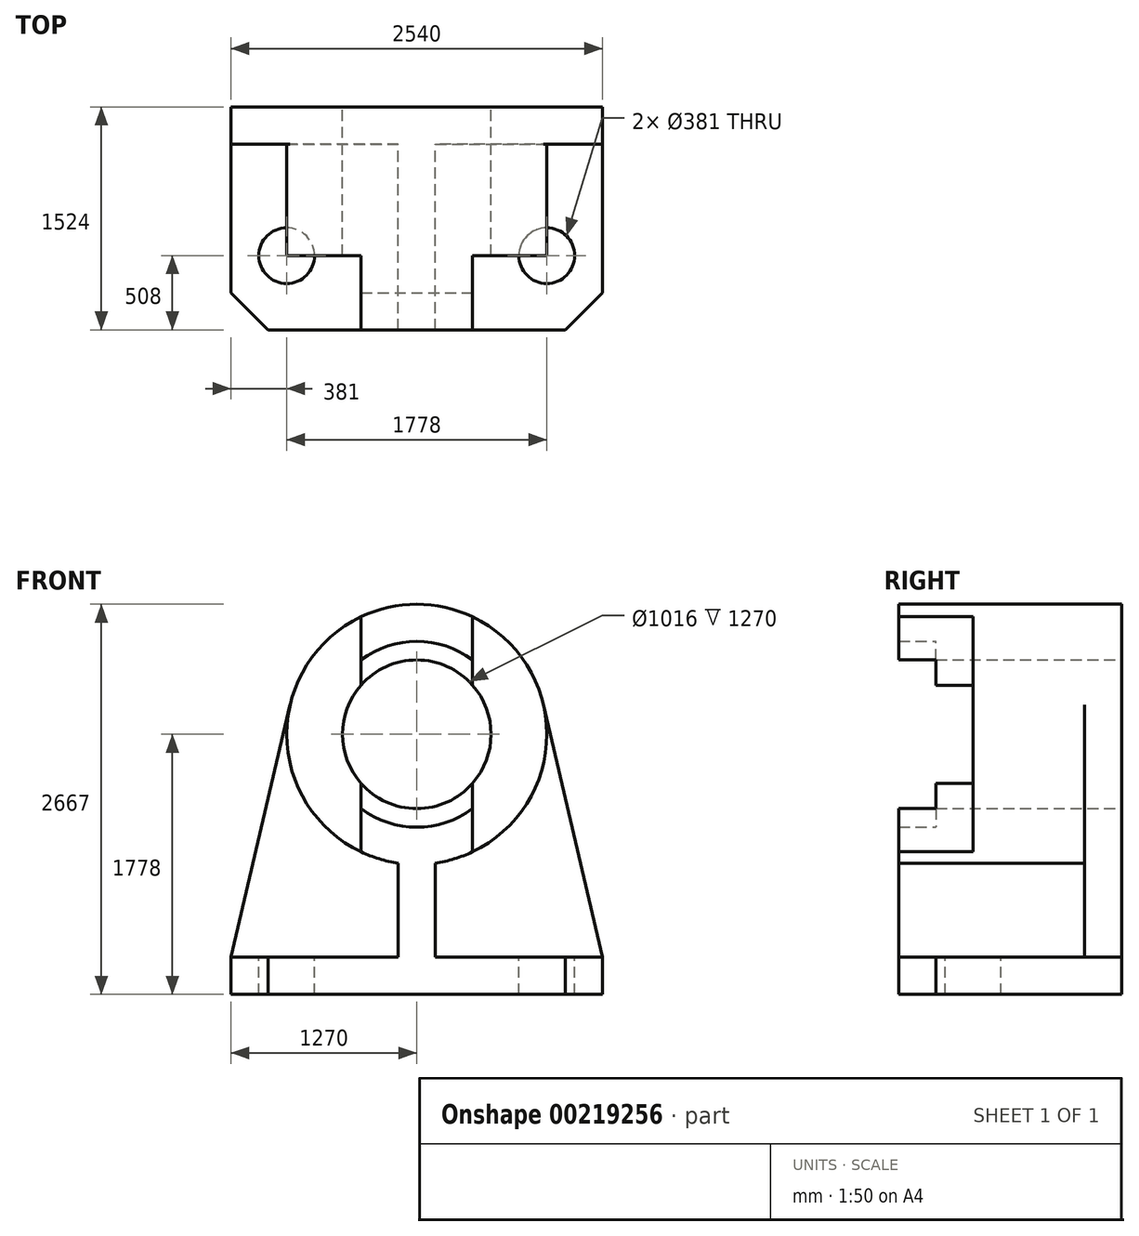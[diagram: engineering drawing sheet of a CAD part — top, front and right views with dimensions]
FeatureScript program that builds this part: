
annotation { "Feature Type Name" : "Feature", "Feature Type Description" : "" }
export const myFeature = defineFeature(function(context is Context, id is Id, definition is map)
    precondition{}
    {
        {
            var Q0;
            Q0=qCreatedBy(makeId("Front.planeOp"),FACE);
            var sketch = newSketch(context, id + "F0", { "sketchPlane" : qUnion([Q0])});
            skCircle(sketch, "E0", {"center": v(0, 0) * mm, "radius": 889 * mm});
            skLineSegment(sketch, "E1.bottom", {"start": v(1270, -1524) * mm, "end": v(-1270, -1524) * mm});
            skLineSegment(sketch, "E1.top", {"start": v(1270, -1778) * mm, "end": v(-1270, -1778) * mm});
            skLineSegment(sketch, "E1.left", {"start": v(1270, -1524) * mm, "end": v(1270, -1778) * mm});
            skLineSegment(sketch, "E1.right", {"start": v(-1270, -1524) * mm, "end": v(-1270, -1778) * mm});
            skPoint(sketch, "E1.middle", {"position": v(0, -1651) * mm});
            skLineSegment(sketch, "E2", {"start": v(-127, -1524) * mm, "end": v(-127, -879.88) * mm});
            skLineSegment(sketch, "E3", {"start": v(127, -879.88) * mm, "end": v(127, -1524) * mm});
            skLineSegment(sketch, "E4", {"start": v(-1270, -1524) * mm, "end": v(-865.58, 202.73) * mm});
            skLineSegment(sketch, "E5", {"start": v(1270, -1524) * mm, "end": v(865.58, 202.73) * mm});
            skCircle(sketch, "E6", {"center": v(0, 0) * mm, "radius": 508 * mm});
            skCircle(sketch, "E7", {"center": v(0, 0) * mm, "radius": 635 * mm});
            skLineSegment(sketch, "E8", {"start": v(-381, 803.22) * mm, "end": v(-381, 336.01) * mm});
            skLineSegment(sketch, "E9", {"start": v(0, 0) * mm, "end": v(0, -2312.44) * mm, "construction": true});
            skLineSegment(sketch, "E10.MirrorCS", {"start": v(381, 803.22) * mm, "end": v(381, 336.01) * mm});
            skPoint(sketch, "E11.orphan", {"position": v(-381, 0) * mm});
            skPoint(sketch, "E12.orphan", {"position": v(381, 0) * mm});
            skLineSegment(sketch, "E13.trimOffspring", {"start": v(-381, -336.01) * mm, "end": v(-381, -803.22) * mm});
            skLineSegment(sketch, "E14.trimOffspring", {"start": v(381, -336.01) * mm, "end": v(381, -803.22) * mm});
            skSolve(sketch);
        }
        {
            var Q0;
            Q0=makeQuery(id+"F0.imprint","IMPRINT",FACE,{"disambiguationData":[TD([[makeQuery(id+"F0.imprint","IMPRINT",EDGE,{"derivedFrom":sQuery(id+"F0.wireOp",EDGE,"E1.top")}),-1.0]])]});
            extrude(context, id + "F1", {"entities" : qUnion([Q0]), "depth" : 1524 * mm});
        }
        {
            var Q0;
            {var subQ0=sQuery(id+"F0.wireOp",EDGE,"E1.left");var subQ3=sQuery(id+"F0.wireOp",EDGE,"E1.bottom");Q0=makeQuery(id+"FlAST3BG48jp0o8_1.boolean.opBoolean","SPLIT",FACE,{"disambiguationData":[TD([makeQuery(id+"F1.opExtrude","SWEPT_FACE",FACE,{"disambiguationData":[OSD([subQ0])]})])],"derivedFrom":makeQuery(id+"F1.opExtrude","SWEPT_FACE",FACE,{"disambiguationData":[OSD([subQ3])]})});}
            var sketch = newSketch(context, id + "F2", { "sketchPlane" : qUnion([Q0])});
            skCircle(sketch, "E15", {"center": v(889, -1016) * mm, "radius": 190.5 * mm});
            skLineSegment(sketch, "E16", {"start": v(0, 0) * mm, "end": v(0, -1627.47) * mm, "construction": true});
            skCircle(sketch, "E17.MirrorC", {"center": v(-889, -1016) * mm, "radius": 190.5 * mm});
            skSolve(sketch);
        }
        {
            var Q0;
            {var subQ0=sQuery(id+"F0.wireOp",EDGE,"E3");Q0=makeQuery(id+"F0.imprint","IMPRINT",FACE,{"disambiguationData":[TD([[makeQuery(id+"F0.imprint","IMPRINT",EDGE,{"derivedFrom":subQ0}),1.0]])]});}
            var Q1;
            {var subQ0=sQuery(id+"F0.wireOp",EDGE,"E2");Q1=makeQuery(id+"F0.imprint","IMPRINT",FACE,{"disambiguationData":[TD([[makeQuery(id+"F0.imprint","IMPRINT",EDGE,{"derivedFrom":subQ0}),1.0]])]});}
            extrude(context, id + "F3", {"entities" : qUnion([Q0, Q1]), "operationType" : NewBodyOperationType.ADD, "depth" : 254 * mm});
        }
        {
            var Q0;
            {var subQ0=sQuery(id+"F0.wireOp",EDGE,"E2");Q0=makeQuery(id+"F0.imprint","IMPRINT",FACE,{"disambiguationData":[TD([[makeQuery(id+"F0.imprint","IMPRINT",EDGE,{"derivedFrom":subQ0}),-1.0]])]});}
            var Q1;
            {var subQ5=sQuery(id+"F0.wireOp",EDGE,"E0");var subQ9=makeQuery(id+"F0.imprint","INTERSECT",VERTEX,{"derivedFrom":[subQ5,sQuery(id+"F0.wireOp",EDGE,"E2")]});Q1=makeQuery(id+"F0.imprint","IMPRINT",FACE,{"disambiguationData":[TD([[makeQuery(id+"F0.imprint","IMPRINT",EDGE,{"disambiguationData":[TD([[subQ9,1.0]])],"derivedFrom":subQ5}),1.0]])]});}
            extrude(context, id + "F4", {"entities" : qUnion([Q0, Q1]), "operationType" : NewBodyOperationType.ADD, "depth" : 1524 * mm});
        }
        {
            var Q0;
            {var subQ1=sQuery(id+"F0.wireOp",EDGE,"E0");var subQ7=makeQuery(id+"F0.imprint","INTERSECT",VERTEX,{"derivedFrom":[subQ1,sQuery(id+"F0.wireOp",EDGE,"E5")]});Q0=makeQuery(id+"F0.imprint","IMPRINT",FACE,{"disambiguationData":[TD([[makeQuery(id+"F0.imprint","IMPRINT",EDGE,{"disambiguationData":[TD([[subQ7,-1.0]])],"derivedFrom":subQ1}),1.0]])]});}
            var Q1;
            {var subQ0=sQuery(id+"F0.wireOp",EDGE,"E10.MirrorCS");var subQ1=sQuery(id+"F0.wireOp",EDGE,"E6");var subQ2=makeQuery(id+"F0.imprint","INTERSECT",VERTEX,{"derivedFrom":[subQ1,subQ0]});Q1=makeQuery(id+"F0.imprint","IMPRINT",FACE,{"disambiguationData":[TD([[makeQuery(id+"F0.imprint","IMPRINT",EDGE,{"disambiguationData":[TD([[subQ2,1.0]])],"derivedFrom":subQ1}),-1.0]])]});}
            var Q2;
            {var subQ0=sQuery(id+"F0.wireOp",EDGE,"E8");var subQ1=sQuery(id+"F0.wireOp",EDGE,"E6");var subQ2=makeQuery(id+"F0.imprint","INTERSECT",VERTEX,{"derivedFrom":[subQ1,subQ0]});Q2=makeQuery(id+"F0.imprint","IMPRINT",FACE,{"disambiguationData":[TD([[makeQuery(id+"F0.imprint","IMPRINT",EDGE,{"disambiguationData":[TD([[subQ2,-1.0]])],"derivedFrom":subQ1}),-1.0]])]});}
            var Q3;
            {var subQ1=sQuery(id+"F0.wireOp",EDGE,"E0");var subQ7=makeQuery(id+"F0.imprint","INTERSECT",VERTEX,{"derivedFrom":[subQ1,sQuery(id+"F0.wireOp",EDGE,"E4")]});Q3=makeQuery(id+"F0.imprint","IMPRINT",FACE,{"disambiguationData":[TD([[makeQuery(id+"F0.imprint","IMPRINT",EDGE,{"disambiguationData":[TD([[subQ7,1.0]])],"derivedFrom":subQ1}),1.0]])]});}
            extrude(context, id + "F5", {"entities" : qUnion([Q0, Q1, Q2, Q3]), "operationType" : NewBodyOperationType.ADD, "depth" : 1016 * mm});
        }
        {
            var Q0;
            {var subQ0=sQuery(id+"F0.wireOp",EDGE,"E13.trimOffspring");var subQ1=sQuery(id+"F0.wireOp",EDGE,"E6");var subQ2=makeQuery(id+"F0.imprint","INTERSECT",VERTEX,{"derivedFrom":[subQ1,subQ0]});Q0=makeQuery(id+"F0.imprint","IMPRINT",FACE,{"disambiguationData":[TD([[makeQuery(id+"F0.imprint","IMPRINT",EDGE,{"disambiguationData":[TD([[subQ2,-1.0]])],"derivedFrom":subQ1}),-1.0]])]});}
            var Q1;
            {var subQ0=sQuery(id+"F0.wireOp",EDGE,"E8");var subQ1=sQuery(id+"F0.wireOp",EDGE,"E6");var subQ2=makeQuery(id+"F0.imprint","INTERSECT",VERTEX,{"derivedFrom":[subQ1,subQ0]});Q1=makeQuery(id+"F0.imprint","IMPRINT",FACE,{"disambiguationData":[TD([[makeQuery(id+"F0.imprint","IMPRINT",EDGE,{"disambiguationData":[TD([[subQ2,1.0]])],"derivedFrom":subQ1}),-1.0]])]});}
            extrude(context, id + "F6", {"entities" : qUnion([Q0, Q1]), "operationType" : NewBodyOperationType.ADD, "depth" : 1270 * mm});
        }
        {
            var Q0;
            {var subQ0=sQuery(id+"F0.wireOp",EDGE,"E8");var subQ1=sQuery(id+"F0.wireOp",EDGE,"E0");var subQ2=makeQuery(id+"F0.imprint","INTERSECT",VERTEX,{"derivedFrom":[subQ1,subQ0]});Q0=makeQuery(id+"F0.imprint","IMPRINT",FACE,{"disambiguationData":[TD([[makeQuery(id+"F0.imprint","IMPRINT",EDGE,{"disambiguationData":[TD([[subQ2,1.0]])],"derivedFrom":subQ1}),1.0]])]});}
            extrude(context, id + "F7", {"entities" : qUnion([Q0]), "operationType" : NewBodyOperationType.ADD, "depth" : 1524 * mm});
        }
        {
            var Q0;
            Q0 = qSketchRegion(id + "F2", true);
            extrude(context, id + "F8", {"entities" : qUnion([Q0]), "operationType" : NewBodyOperationType.REMOVE, "endBound" : BoundingType.UP_TO_NEXT, "oppositeDirection" : true, "depth" : 25.4 * mm});
        }
        {
            var Q0;
            Q0=makeQuery(id+"F1.opExtrude","CAP_EDGE",EDGE,{"disambiguationData":[OSD([sQuery(id+"F0.wireOp",EDGE,"E1.right")])],"isStart":false});
            var Q1;
            Q1=makeQuery(id+"F1.opExtrude","CAP_EDGE",EDGE,{"disambiguationData":[OSD([sQuery(id+"F0.wireOp",EDGE,"E1.left")])],"isStart":false});
            chamfer(context, id + "F9", {"entities" : qUnion([Q0, Q1]), "width" : 254 * mm, "tangentPropagation" : true});
        }
    });
